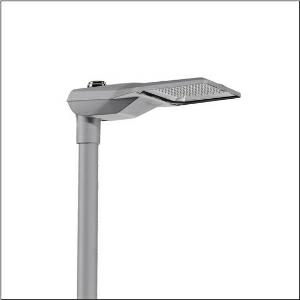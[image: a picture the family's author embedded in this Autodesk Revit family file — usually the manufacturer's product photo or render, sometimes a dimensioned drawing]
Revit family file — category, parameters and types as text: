
# Revit family: streetlight_sl_21_midi___st1_0a_5xe7d27n08nb_1197
name_source: partatom
category: Lighting Fixtures
units: mm (PartAtom-declared; Revit-internal decimal feet)

## family parameters
Cut with Voids When Loaded = No
Host = Face
Light Source = No
Part Type = Normal
Room Calculation Point = No
Round Connector Dimension = Use Diameter
Shared = No

## types (1)
- --- (1 x LED, 18780 lm, 151.2 W, 2200K)
    Apparent Load = 151 VA
    CIE Flux Codes = 40 73 97 100 100
    Color Rendering = 70
    Color Temperature = 2200K
    Default Elevation = 1800 mm
    Description = Streetlight SL 21 midi, mast luminaire, primary light control with lens, of PMMA, primary optical cover: cover, of toughened safety glass, transparent, light distribution: ST1.0a, light emission: direct distribution, primary light characteristic: asymmetric, installation type: side-entry, LED, 3G 2.5mm², High Power LED, rated luminous flux: 18.780lm, luminous efficacy: 124lm/W, light colour: 722, colour temperature: 2200K, control gear: NEMA (7pin), control: overheat protection, pre-setting: linear dimming characteristic, constant luminous flux control, time-dependent luminous flux control, flexible luminous flux parameterisation, mains connection: 220..240V, AC, 50/60Hz, connection cable pre-assembled, cable length: 12,5m, wiring characteristics: H05VV-F, start of lifetime: 151W, end of service life: 157W, reduction: 70W, luminaire housing, of diecast aluminium (EN AC-44300), powder-coated, Siteco® metallic grey (DB 702S), corrosivity category C5 mid according to DIN EN ISO 12944, multi-level sealing system, sealing non-destructively replaceable, inclination adjustable: 0°, 5°, 10°, 15°, length: 644mm, width: 335mm, height: 110mm, spigot size: 42mm (side-entry), mounting height: 4..8m, protection rating (complete): IP66, insulation class (complete): insulation class I (protective earthing), certification: CE, ENEC, ENEC+, VDE, impact resistance: IK10, permissible operating ambient temperature for outdoor applications: -40..+50°C, standard-compliant lighting for roads and squares, packaging unit: 1 piece

Light Distribution: ST1.0a
    Height = 111 mm
    Lamp = 1 x LED
    Lamp Light Flux = 18780 lm
    Lamp Power = 151.2 W
    Lamp count = 1
    Length = 644 mm
    Luminous efficacy = 124 lm/W
    Manufacturer = Siteco
    ModVariant = No
    Model = 5XE7D27N08NB
    Number of Poles = 1
    OnlyDefault = Yes
    Power Factor = 1
    Product Name = Streetlight SL 21 midi | ST1.0a
    Product group = mast luminaire | pylon top
    ProductGroupID = 6100
    Protection Class = Protection class I
    Protection Degree = IP 66
    RLX_Detail_Level = 1
    RLX_Emergency_Light_Flux = 0 lm
    RLX_Emergency_Type = 0
    RLX_Emergency_Type_DB = No
    RlxData = <blob elided: 26597 chars, md5=2f9351fd>
    Socket = socket
    Standby Power = 0 W
    System Light Flux = 18781 lm
    System Power = 151 W
    Type Comments = factory setting: luminous flux: 100 % | dim-lin: 254 | 802 mA
    Type Image = l_1294377.jpg
    URL = http://relux.com
    VarID = @adj_156683
    Voltage = 0 V
    Weight = 0.00 kg
    Width = 336 mm

## geometry (parser evidence)
native form markers: Blend x4, Sweep x10
no freeform markers — native parametric forms only
